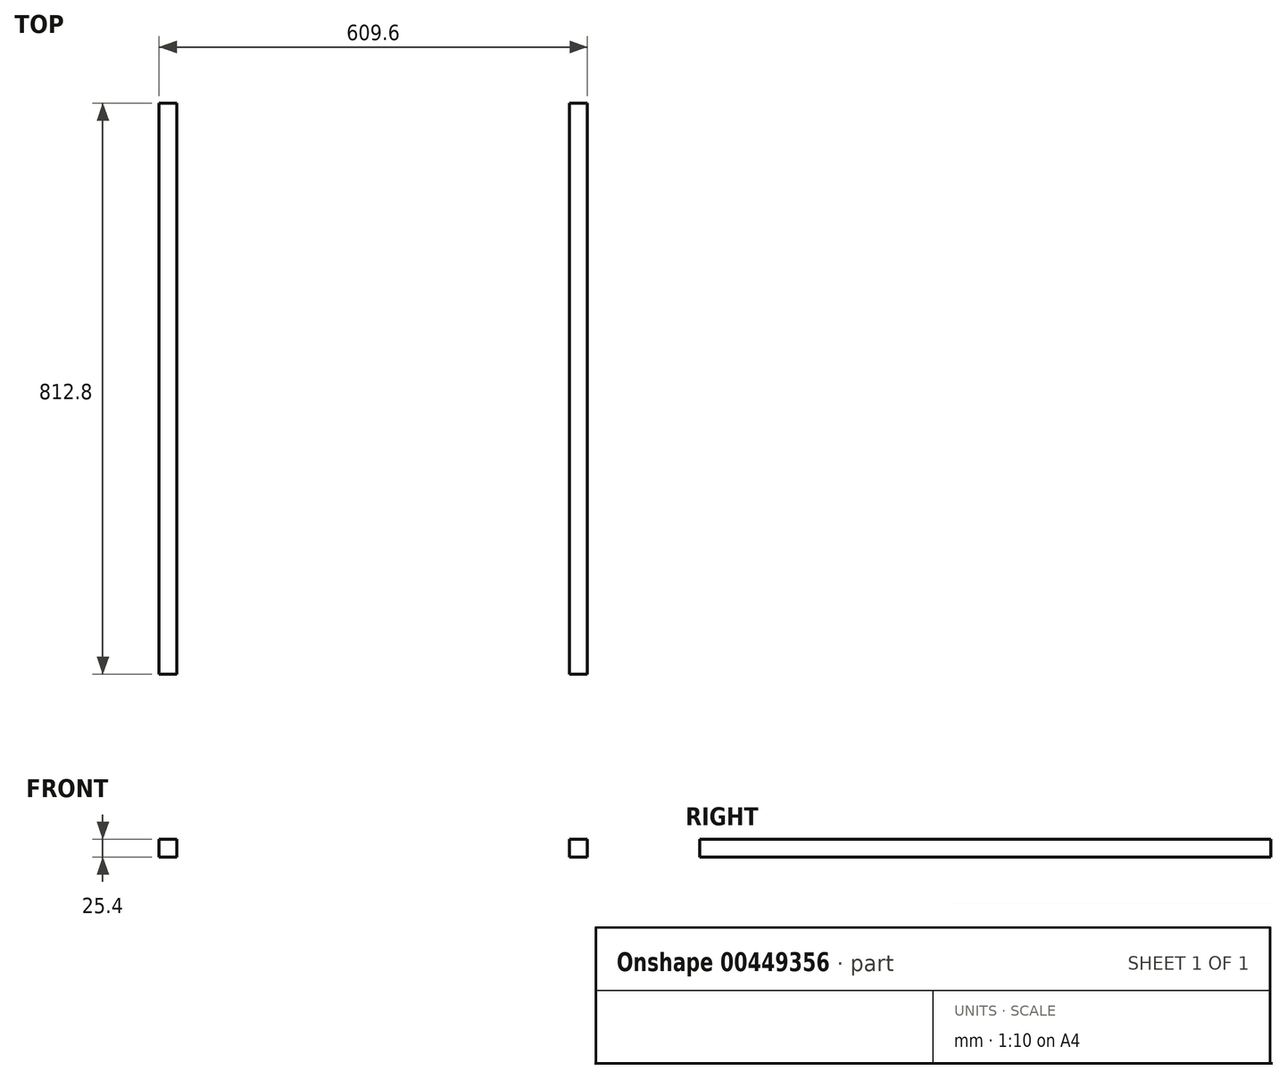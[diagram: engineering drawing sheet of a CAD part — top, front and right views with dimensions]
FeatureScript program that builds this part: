
annotation { "Feature Type Name" : "Feature", "Feature Type Description" : "" }
export const myFeature = defineFeature(function(context is Context, id is Id, definition is map)
    precondition{}
    {
        {
            var Q0;
            Q0=qCreatedBy(makeId("Front.planeOp"),FACE);
            var sketch = newSketch(context, id + "F0", { "sketchPlane" : qUnion([Q0])});
            skLineSegment(sketch, "E0.bottom", {"start": v(-304.8, 0) * mm, "end": v(-279.4, 0) * mm});
            skLineSegment(sketch, "E0.top", {"start": v(-304.8, -25.4) * mm, "end": v(-279.4, -25.4) * mm});
            skLineSegment(sketch, "E0.left", {"start": v(-304.8, 0) * mm, "end": v(-304.8, -25.4) * mm});
            skLineSegment(sketch, "E0.right", {"start": v(-279.4, 0) * mm, "end": v(-279.4, -25.4) * mm});
            skLineSegment(sketch, "E1.bottom", {"start": v(279.4, 0) * mm, "end": v(304.8, 0) * mm});
            skLineSegment(sketch, "E1.top", {"start": v(279.4, -25.4) * mm, "end": v(304.8, -25.4) * mm});
            skLineSegment(sketch, "E1.left", {"start": v(279.4, 0) * mm, "end": v(279.4, -25.4) * mm});
            skLineSegment(sketch, "E1.right", {"start": v(304.8, 0) * mm, "end": v(304.8, -25.4) * mm});
            skLineSegment(sketch, "E2", {"start": v(-279.4, 0) * mm, "end": v(279.4, 0) * mm});
            skSolve(sketch);
        }
        {
            var Q0;
            Q0=makeQuery(id+"F0.imprint","IMPRINT",FACE,{"disambiguationData":[TD([[makeQuery(id+"F0.imprint","IMPRINT",EDGE,{"derivedFrom":sQuery(id+"F0.wireOp",EDGE,"E0.bottom")}),-1.0]])]});
            var Q1;
            Q1=makeQuery(id+"F0.imprint","IMPRINT",FACE,{"disambiguationData":[TD([[makeQuery(id+"F0.imprint","IMPRINT",EDGE,{"derivedFrom":sQuery(id+"F0.wireOp",EDGE,"E1.bottom")}),-1.0]])]});
            extrude(context, id + "F1", {"entities" : qUnion([Q0, Q1]), "depth" : 812.8 * mm});
        }
    });
